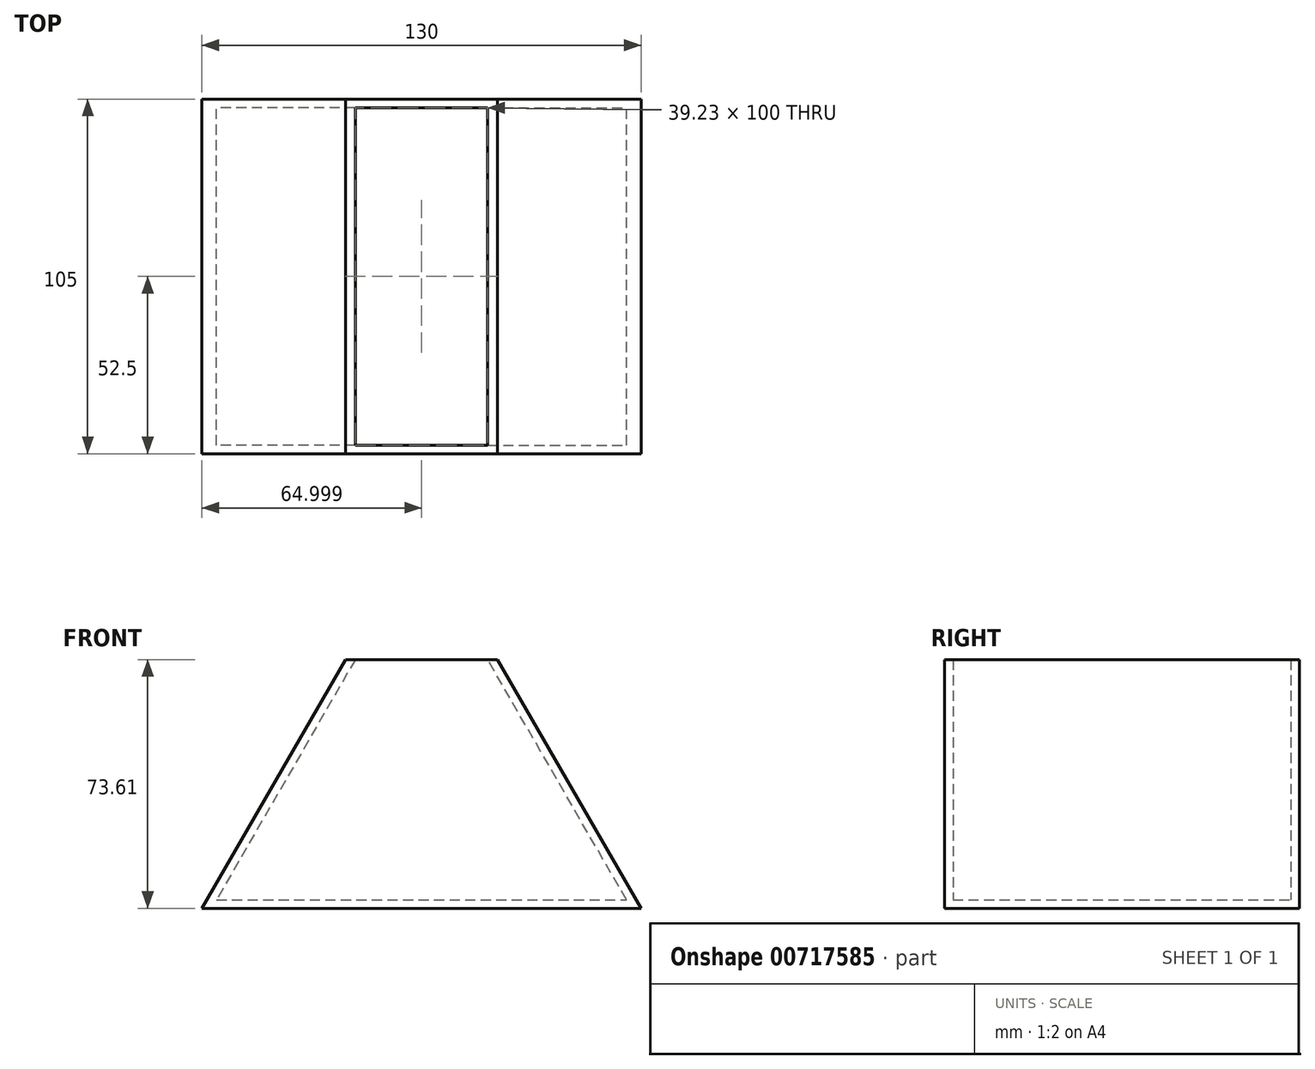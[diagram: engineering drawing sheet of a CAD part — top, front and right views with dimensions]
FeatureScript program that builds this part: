
annotation { "Feature Type Name" : "Feature", "Feature Type Description" : "" }
export const myFeature = defineFeature(function(context is Context, id is Id, definition is map)
    precondition{}
    {
        {
            var Q0;
            Q0=qCreatedBy(makeId("Front.planeOp"),FACE);
            var sketch = newSketch(context, id + "F0", { "sketchPlane" : qUnion([Q0])});
            skLineSegment(sketch, "E0", {"start": v(-90.96, 0) * mm, "end": v(39.04, 0) * mm});
            skLineSegment(sketch, "E1", {"start": v(39.04, 0) * mm, "end": v(-3.46, 73.61) * mm});
            skLineSegment(sketch, "E2", {"start": v(-3.46, 73.61) * mm, "end": v(-48.46, 73.61) * mm});
            skLineSegment(sketch, "E3", {"start": v(-48.46, 73.61) * mm, "end": v(-90.96, 0) * mm});
            skSolve(sketch);
        }
        {
            var Q0;
            Q0=qSketchRegion(id+"F0",true);
            var Q1;
            Q1=makeQuery(id+"F0.imprint","IMPRINT",FACE,{"disambiguationData":[TD([[makeQuery(id+"F0.imprint","IMPRINT",EDGE,{"derivedFrom":sQuery(id+"F0.wireOp",EDGE,"E0")}),1.0]])]});
            extrude(context, id + "F1", {"entities" : qUnion([Q0, Q1]), "depth" : 105 * mm});
        }
        {
            var Q0;
            Q0=makeQuery(id+"F1.opExtrude","SWEPT_FACE",FACE,{"disambiguationData":[OSD([sQuery(id+"F0.wireOp",EDGE,"E2")])]});
            shell(context, id + "F2", {"entities" : qUnion([Q0]), "thickness" : 2.5 * mm});
        }
    });
